# Revit family: Camera-Security-Panasonic-Super_Dynamic-Weatherproof-H265-AI-Network-X1551LNSeriesY
name_source: partatom
category: Security Devices
units: mm (PartAtom-declared; Revit-internal decimal feet)

## family parameters
Cut with Voids When Loaded = No
Host = Face
Maintain Annotation Orientation = No
OmniClass Number = 23.85.10.14.11
OmniClass Title = Cameras
Part Type = Normal
Room Calculation Point = No
Round Connector Dimension = Use Diameter
Shared = No

## types (2) — shared parameters
4K = Resolution : 4K
5M = Resolution : 5M
Alarm Input Or Output Specification = ALARM IN 1(Alarm input 1/ Black & white input/ Auto time adjustment input) (x1), ALARM IN 2 (Alarm input 2/ ALARM OUT) (x1), ALARM IN 3 (Alarm input 3/ AUX OUT) (x1)
Audio In = Yes
Audio Out = Yes
Communication Ports = 10Base-T / 100Base-TX, RJ45 connector
Day Or Night = Yes
Equipment Abbreviation = SC
Family Version = 1.0.0
Full HD = Resolution : Full HD
Has POE = Yes
Height = 5.23622 "
IP Or Analog = IP
Indoor Or Outdoor = Outdoor
Manufacturer = Panasonic
Model Disclaimer = Contact Panasonic for more information
Mounting Positions = Mount Dependent or Surface Mount
Operational Humidity = 10 to 100 % (no condensation)
Operational Temperature = -40 °F to 140 °F
Panning Range = -180 to +180
Power Active = 11.2 W
Product Documentation Link = https://bizpartner.panasonic.net
Product Material = Paint - Panasonic -i-Pro White
Product Page URL = https://security.panasonic.com
Provide Feedback = https://www.surveymonkey.com
Regulatory Compliance = UL (UL60950-1), c-UL (CSA C22.2 No.60950-1), CE, IEC60950-1, FCC (Part15 ClassA), ICES003 ClassA, EN55032 ClassB, EN55024
Shock Resistance = IK10 (IEC 62262)
Storage Temperature = -40 °F to 140 °F
Super Dynamic Range = Yes
Tilting Range = -100 to +100
URL = http://security.panasonic.com
Vandal Resistant = Yes
Voltage DC = 12 V
WQHD = Resolution : WQHD
Water and Dust Resistance = IP66 (IEC60529), Type 4X (UL50E), NEMA 4X compliant
Width = 5.23622 "
Yaw Max = 100.00°
Yaw Min = -190.00°
Yawing Range = -190 to +100
z Base Square = Yes
z Camera Center Offset = 0.2874 "
z Camera Center Offset Base = 1.1811 "
z Column Height = 3.11024 "
z Const CameraYawAxis = 15.74803 "
z Const Pan Handle Length = 27.55906 "
z Const Tilt Base Length = 9.84252 "
z Const Tilt Base2 Length = 19.68504 "
z Const Tilt Handle Length = 14.17323 "
z Const Yaw Axis Length = 7.87402 "
z Const Yaw Base Length = 10.23622 "
z Const Yaw Base2 Length = 17.32283 "
z Const Yaw Handle Length = 9.25197 "
z Hinge Height = 3.79921 "
zero-valued in all types: Default Elevation

## per-type parameters (varying)
| type | Angle Of View | Camera Number | Date Last Modified | Description | HFOV Max 169 | HFOV Max 43 | HFOV Min 169 | HFOV Min 43 | Minimum Illumination | Part Description | VFOV Max 169 | VFOV Max 43 | VFOV Min 169 | VFOV Min 43 | z VV Viewpoint Depth Max | z VV Viewpoint Depth Min |
| WV-X1551LN | 106 | 1551 | 2020/05/12 | Security Camera, Super Dynamic, H.265, 5M, Weatherproof, AI, Network, WV-X1551LN | 106.00° | 106.00° | 34.00° | 34.00° | 0.070 lx | Security Camera, Super Dynamic, H.265, 5M, Weatherproof, AI, Network, WV-X1551LN | 57.00° | 57.00° | 19.00° | 19.00° | 6.44094 " | 6.44094 " |
| WV-X1571LN | 104 | 1571 | 2020/08/25 | Security Camera, Super Dynamic, H.265, 4K, Weatherproof, AI, Network, WV-X1571LN | 104.00° | 104.00° | 53.00° | 53.00° | 0.090 lx | Security Camera, Super Dynamic, H.265, 4K, Weatherproof, AI, Network, WV-X1571LN | 56.00° | 56.00° | 30.00° | 30.00° | 8.26772 " | 8.26772 " |

note: column(s) folded — value = type name in every type: Model, Part Number

## geometry (parser evidence)
native form markers: Blend x2, Sweep x8
no freeform markers — native parametric forms only
